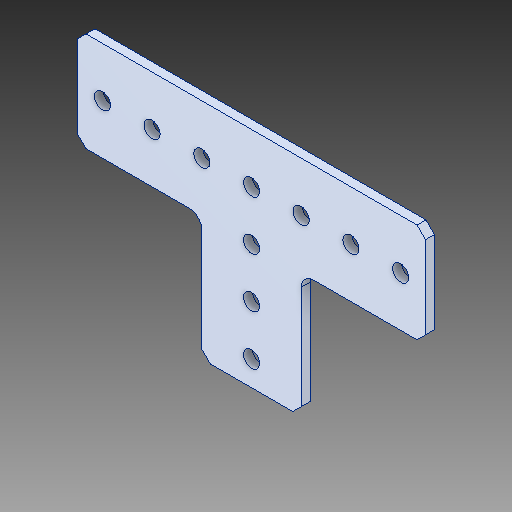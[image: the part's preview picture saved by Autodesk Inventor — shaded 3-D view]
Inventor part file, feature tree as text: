
AUTODESK INVENTOR PART (.ipt)
format: ipt  version: 2017 (Build 210142000, 142)  size: 128,512 bytes
history: native  units: in
note: dims shown in document units (in); Inventor stores cm internally (conversion verified against a paired STEP export)
features: fillet x1
ambient origin geometry x8: Origin, YZ Plane, XZ Plane, XY Plane, X Axis, Y Axis, Z Axis, Center Point
bodies: Solid1 (feature_tree)
feature tree (1):
  fillet  "Fillet1"  [1 undecoded]
note: 1 required parameter value undecoded (feature->parameter linkage not recoverable at this tier; creation-order binding heuristic only, values carry confidence <= 0.55)
